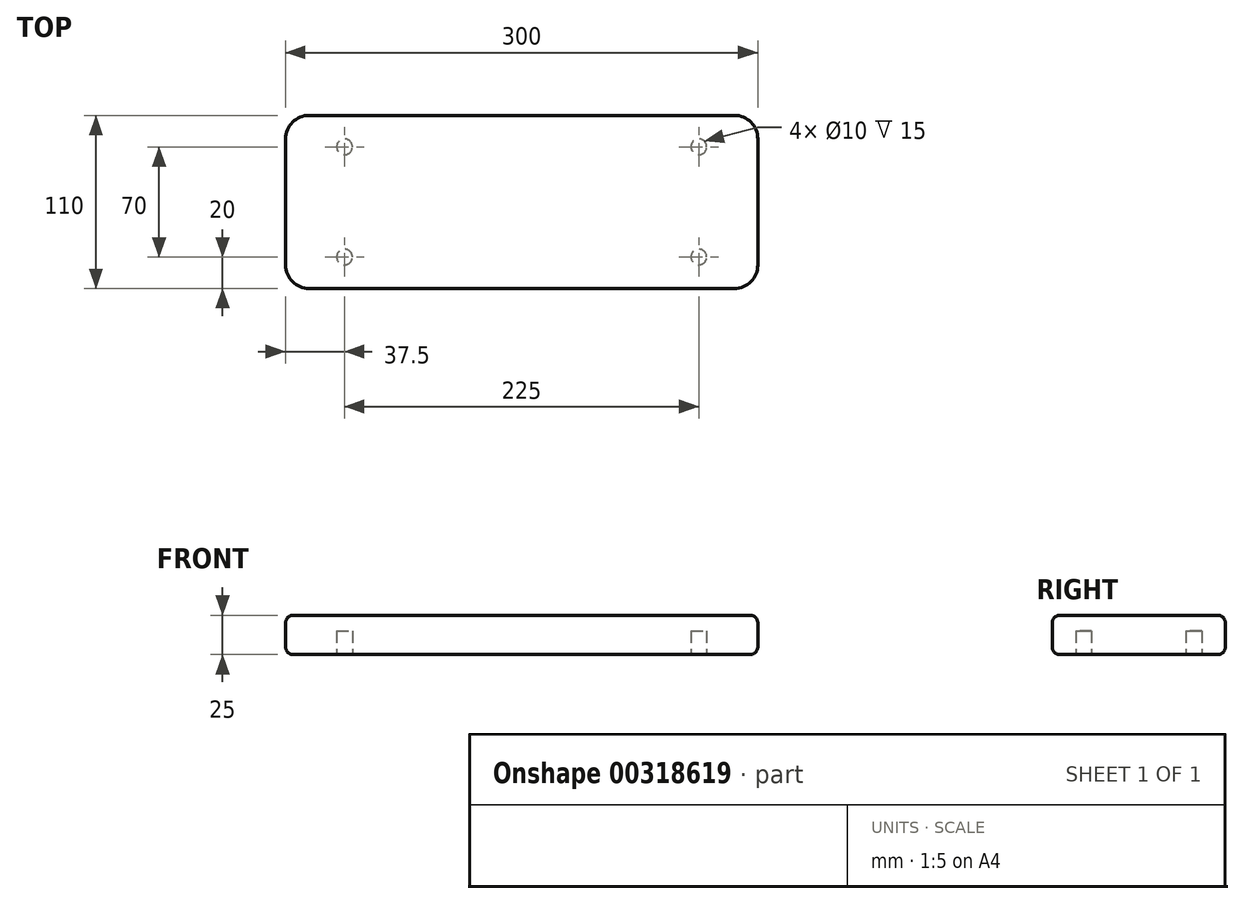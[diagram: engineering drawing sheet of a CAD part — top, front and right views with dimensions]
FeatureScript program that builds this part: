
annotation { "Feature Type Name" : "Feature", "Feature Type Description" : "" }
export const myFeature = defineFeature(function(context is Context, id is Id, definition is map)
    precondition{}
    {
        {
            var Q0;
            Q0=qCreatedBy(makeId("Top.planeOp"),FACE);
            var sketch = newSketch(context, id + "F0", { "sketchPlane" : qUnion([Q0])});
            skLineSegment(sketch, "E0.rect.bottom", {"start": v(150, 55) * mm, "end": v(-150, 55) * mm});
            skLineSegment(sketch, "E0.rect.top", {"start": v(150, -55) * mm, "end": v(-150, -55) * mm});
            skLineSegment(sketch, "E0.rect.left", {"start": v(150, 55) * mm, "end": v(150, -55) * mm});
            skLineSegment(sketch, "E0.rect.right", {"start": v(-150, 55) * mm, "end": v(-150, -55) * mm});
            skPoint(sketch, "E0.rect.middle", {"position": v(0, 0) * mm});
            skSolve(sketch);
        }
        {
            var Q0;
            Q0=qSketchRegion(id+"F0",true);
            extrude(context, id + "F1", {"entities" : qUnion([Q0]), "depth" : 25 * mm});
        }
        {
            var Q0;
            Q0=makeQuery(id+"F1.opExtrude","CAP_FACE",FACE,{"disambiguationData":[OSD([sQuery(id+"F0.wireOp",EDGE,"E0.rect.bottom"),sQuery(id+"F0.wireOp",EDGE,"E0.rect.top"),sQuery(id+"F0.wireOp",EDGE,"E0.rect.left"),sQuery(id+"F0.wireOp",EDGE,"E0.rect.right")])],"isStart":true});
            var sketch = newSketch(context, id + "F2", { "sketchPlane" : qUnion([Q0])});
            skLineSegment(sketch, "E1.rect.bottom", {"start": v(112.5, -35) * mm, "end": v(-112.5, -35) * mm, "construction": true});
            skLineSegment(sketch, "E1.rect.top", {"start": v(112.5, 35) * mm, "end": v(-112.5, 35) * mm, "construction": true});
            skLineSegment(sketch, "E1.rect.left", {"start": v(112.5, -35) * mm, "end": v(112.5, 35) * mm, "construction": true});
            skLineSegment(sketch, "E1.rect.right", {"start": v(-112.5, -35) * mm, "end": v(-112.5, 35) * mm, "construction": true});
            skPoint(sketch, "E1.rect.middle", {"position": v(0, 0) * mm});
            skCircle(sketch, "E2", {"center": v(-112.5, 35) * mm, "radius": 5 * mm});
            skCircle(sketch, "E3", {"center": v(112.5, 35) * mm, "radius": 5 * mm});
            skCircle(sketch, "E4", {"center": v(112.5, -35) * mm, "radius": 5 * mm});
            skCircle(sketch, "E5", {"center": v(-112.5, -35) * mm, "radius": 5 * mm});
            skSolve(sketch);
        }
        {
            var Q0;
            Q0=qSketchRegion(id+"F2",true);
            extrude(context, id + "F3", {"entities" : qUnion([Q0]), "operationType" : NewBodyOperationType.REMOVE, "oppositeDirection" : true, "depth" : 15 * mm});
        }
        {
            var Q0;
            Q0=makeQuery(id+"F1.opExtrude","SWEPT_EDGE",EDGE,{"disambiguationData":[OSD([sQuery(id+"F0.wireOp",EDGE,"E0.rect.bottom"),sQuery(id+"F0.wireOp",EDGE,"E0.rect.right")])]});
            var Q1;
            Q1=makeQuery(id+"F1.opExtrude","SWEPT_EDGE",EDGE,{"disambiguationData":[OSD([sQuery(id+"F0.wireOp",EDGE,"E0.rect.top"),sQuery(id+"F0.wireOp",EDGE,"E0.rect.right")])]});
            var Q2;
            Q2=makeQuery(id+"F1.opExtrude","SWEPT_EDGE",EDGE,{"disambiguationData":[OSD([sQuery(id+"F0.wireOp",EDGE,"E0.rect.top"),sQuery(id+"F0.wireOp",EDGE,"E0.rect.left")])]});
            var Q3;
            Q3=makeQuery(id+"F1.opExtrude","SWEPT_EDGE",EDGE,{"disambiguationData":[OSD([sQuery(id+"F0.wireOp",EDGE,"E0.rect.bottom"),sQuery(id+"F0.wireOp",EDGE,"E0.rect.left")])]});
            fillet(context, id + "F4", {"entities" : qUnion([Q0, Q1, Q2, Q3]), "radius" : 15 * mm, "tangentPropagation" : true, "allowEdgeOverflow" : false});
        }
        {
            var Q0;
            Q0=makeQuery(id+"F1.opExtrude","CAP_EDGE",EDGE,{"disambiguationData":[OSD([sQuery(id+"F0.wireOp",EDGE,"E0.rect.right")])],"isStart":false});
            var Q1;
            Q1=makeQuery(id+"F1.opExtrude","CAP_EDGE",EDGE,{"disambiguationData":[OSD([sQuery(id+"F0.wireOp",EDGE,"E0.rect.right")])],"isStart":true});
            fillet(context, id + "F5", {"entities" : qUnion([Q0, Q1]), "radius" : 5 * mm, "tangentPropagation" : true, "allowEdgeOverflow" : false});
        }
    });
